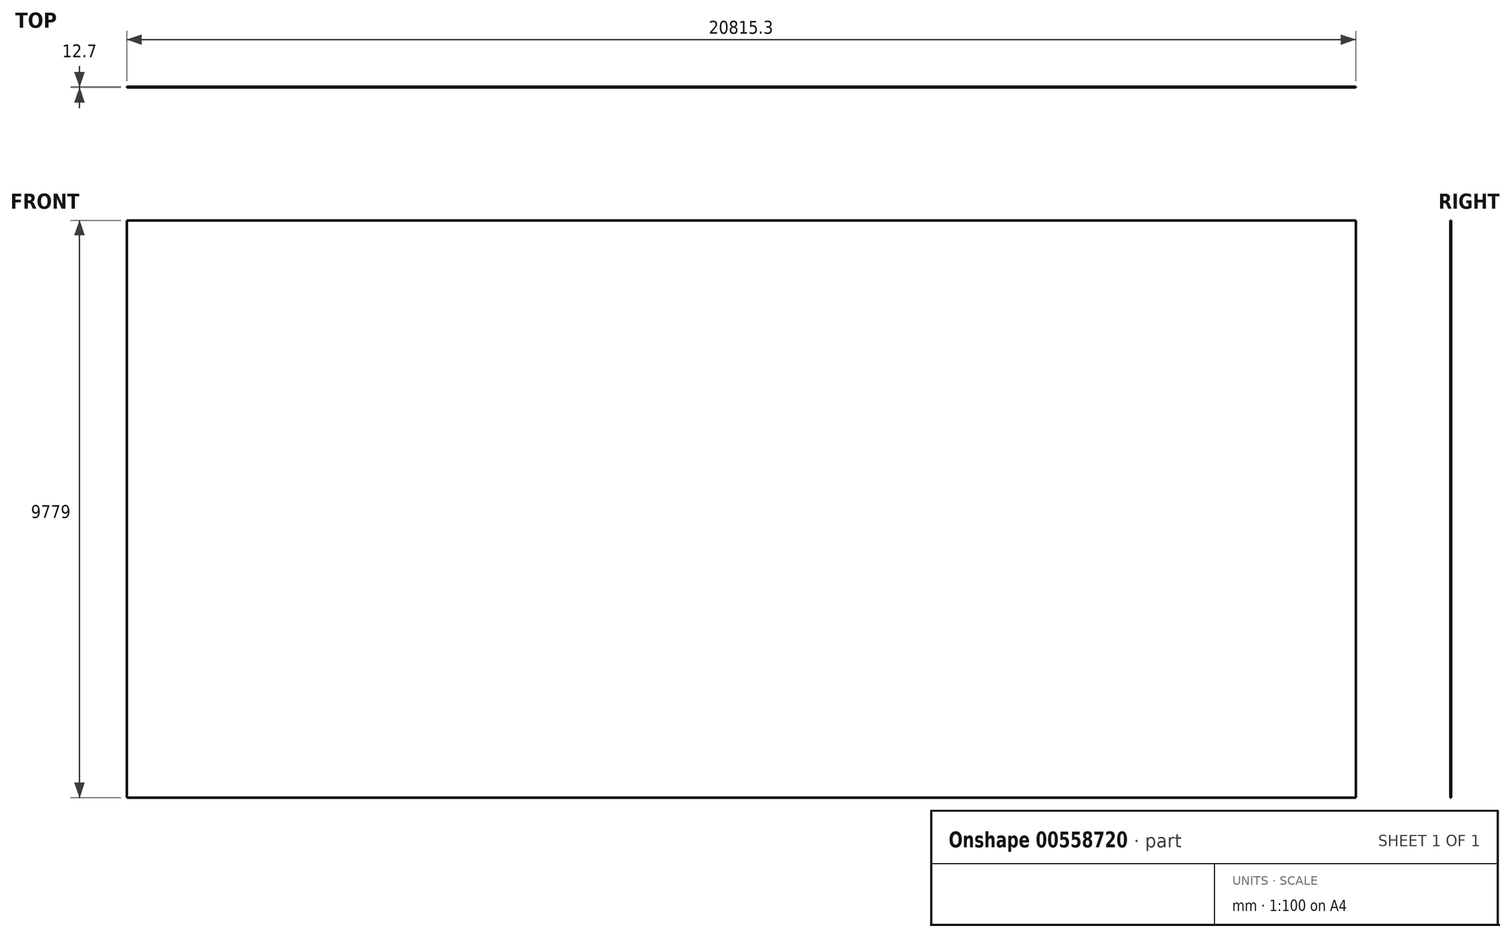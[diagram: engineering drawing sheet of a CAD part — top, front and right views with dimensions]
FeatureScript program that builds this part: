
annotation { "Feature Type Name" : "Feature", "Feature Type Description" : "" }
export const myFeature = defineFeature(function(context is Context, id is Id, definition is map)
    precondition{}
    {
        {
            var Q0;
            Q0=qCreatedBy(makeId("Front.planeOp"),FACE);
            var sketch = newSketch(context, id + "F0", { "sketchPlane" : qUnion([Q0])});
            skLineSegment(sketch, "E0.bottom", {"start": v(0, 0) * mm, "end": v(20815.3, 0) * mm});
            skLineSegment(sketch, "E0.top", {"start": v(0, 9779) * mm, "end": v(20815.3, 9779) * mm});
            skLineSegment(sketch, "E0.left", {"start": v(0, 0) * mm, "end": v(0, 9779) * mm});
            skLineSegment(sketch, "E0.right", {"start": v(20815.3, 0) * mm, "end": v(20815.3, 9779) * mm});
            skSolve(sketch);
        }
        {
            var Q0;
            Q0=qSketchRegion(id+"F0",true);
            extrude(context, id + "F1", {"entities" : qUnion([Q0]), "depth" : 12.7 * mm, "offsetDistance" : 25.4 * mm});
        }
    });
